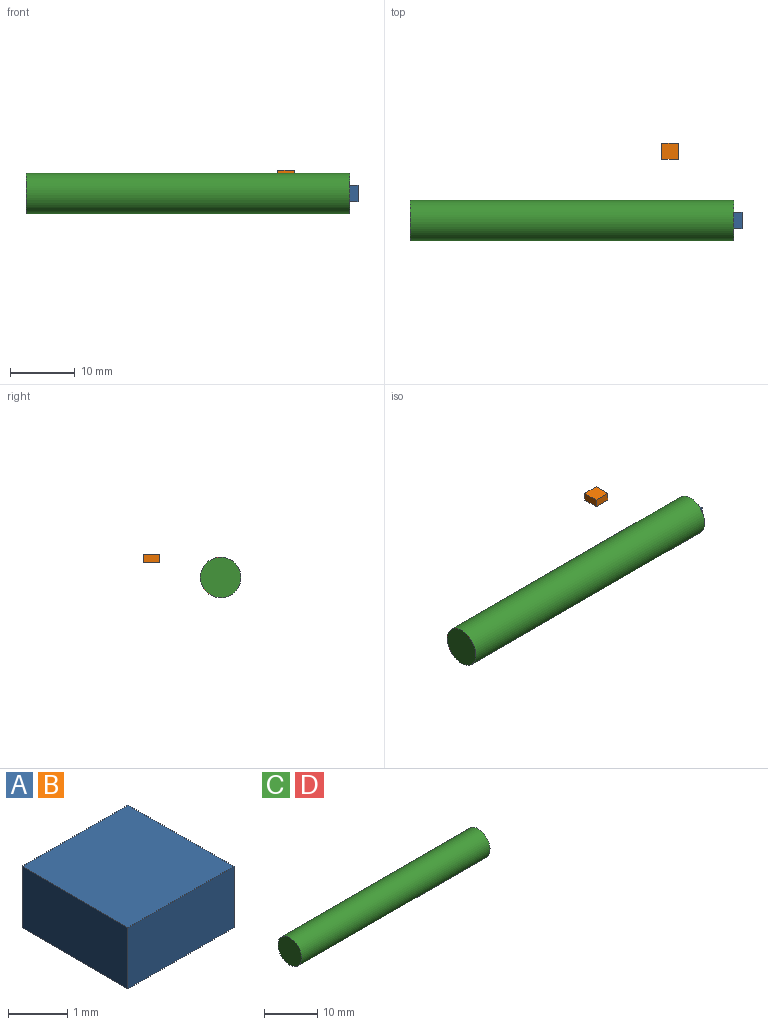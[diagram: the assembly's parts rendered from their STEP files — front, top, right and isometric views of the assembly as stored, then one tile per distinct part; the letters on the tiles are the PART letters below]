
ASSEMBLY  parts=4 mates=1
PART A: 6 faces, bbox 2.5x2.5x1.3 mm
  f0: plane 2.54x1.27mm, normal (0,-1,0), area 3.2mm2, adj f1,f3,f4,f5
  f1: plane 2.54x1.27mm, normal (1,0,0), area 3.2mm2, adj f0,f2,f4,f5
  f2: plane 2.54x1.27mm, normal (0,1,0), area 3.2mm2, adj f1,f3,f4,f5
  f3: plane 2.54x1.27mm, normal (-1,0,0), area 3.2mm2, adj f0,f2,f4,f5
  f4: plane 2.54x2.54mm, normal (0,0,1), area 6.5mm2, adj f0,f1,f2,f3
  f5: plane 2.54x2.54mm, normal (0,0,-1), area 6.5mm2, adj f0,f1,f2,f3
PART B: same geometry as A
PART C: 3 faces, bbox 50x6.3x6.3 mm
  f0: cylinder r=3.13mm len=50mm, axis (-1,0,0), area 983.4mm2, adj f1,f2
  f1: plane 6.26x6.26mm, normal (1,0,0), area 30.8mm2, adj f0
  f2: plane 6.26x6.26mm, normal (-1,0,0), area 30.8mm2, adj f0
PART D: same geometry as C
PLACE A rot(axis=(0.71,0,-0.71),180deg) t=(40.87,5.29,-4.71)mm
PLACE B t=(29.76,16.01,-2.39)mm
PLACE C t=(-10.4,5.29,-4.71)mm
PLACE D t=(-10.4,5.29,-4.71)mm
MATE fastened A.f4 <-> C.f0  axis (-1,0,0) through (39.6,5.29,-4.71)mm
